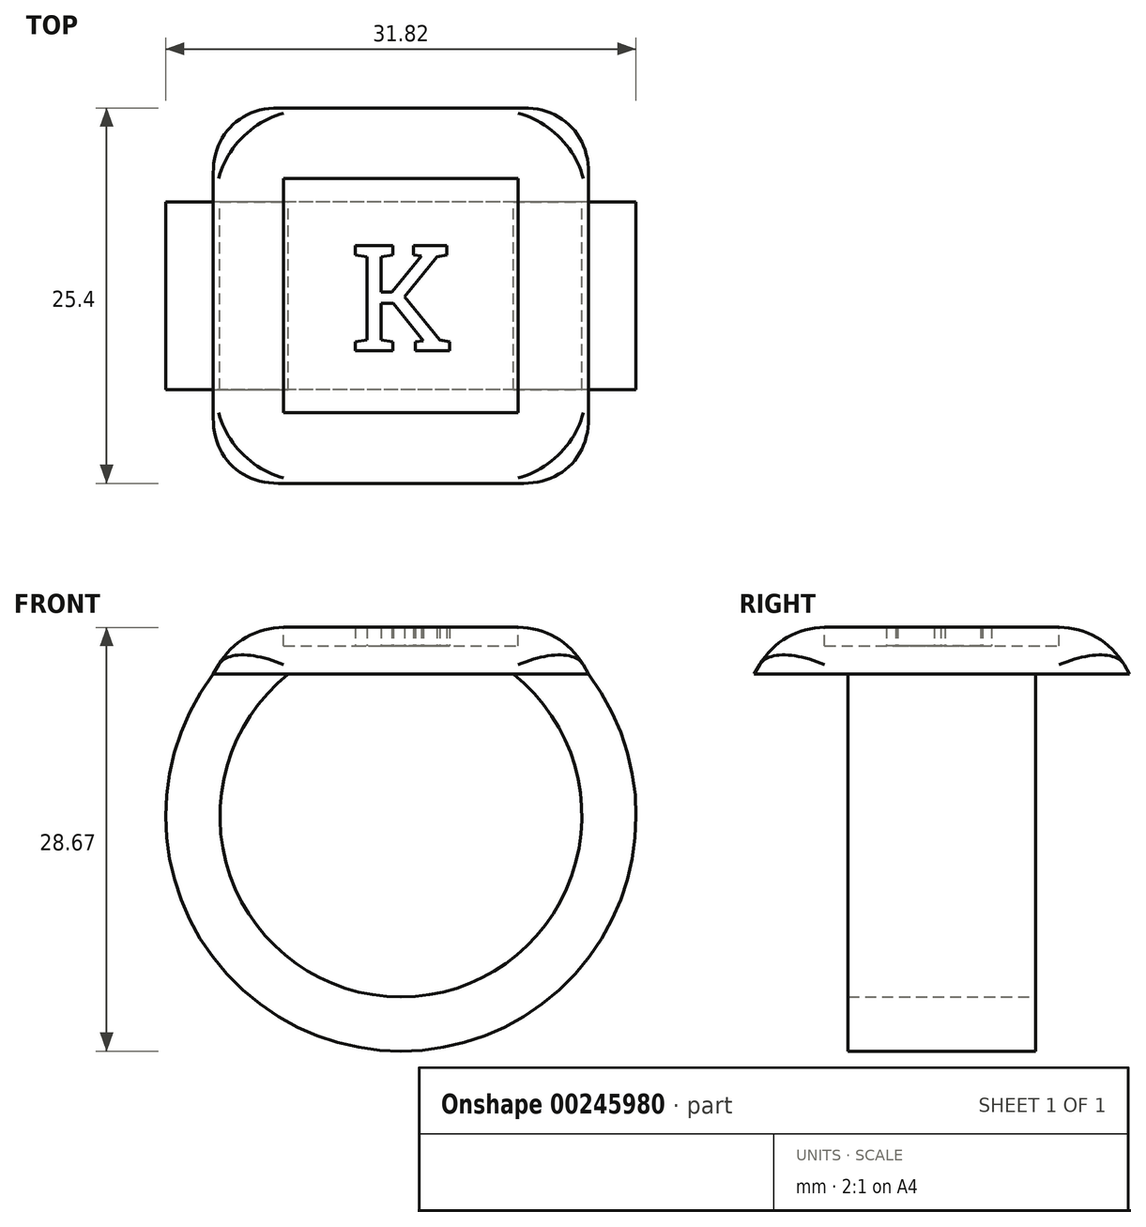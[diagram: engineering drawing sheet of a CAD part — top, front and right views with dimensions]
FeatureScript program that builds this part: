
annotation { "Feature Type Name" : "Feature", "Feature Type Description" : "" }
export const myFeature = defineFeature(function(context is Context, id is Id, definition is map)
    precondition{}
    {
        {
            var Q0;
            Q0=qCreatedBy(makeId("Top.planeOp"),FACE);
            var sketch = newSketch(context, id + "F0", { "sketchPlane" : qUnion([Q0])});
            skLineSegment(sketch, "E0.bottom", {"start": v(12.7, 12.7) * mm, "end": v(-12.7, 12.7) * mm});
            skLineSegment(sketch, "E0.top", {"start": v(12.7, -12.7) * mm, "end": v(-12.7, -12.7) * mm});
            skLineSegment(sketch, "E0.left", {"start": v(12.7, 12.7) * mm, "end": v(12.7, -12.7) * mm});
            skLineSegment(sketch, "E0.right", {"start": v(-12.7, 12.7) * mm, "end": v(-12.7, -12.7) * mm});
            skPoint(sketch, "E0.middle", {"position": v(0, 0) * mm});
            skSolve(sketch);
        }
        {
            var Q0;
            Q0=makeQuery(id+"F0.imprint","IMPRINT",FACE,{"disambiguationData":[TD([[makeQuery(id+"F0.imprint","IMPRINT",EDGE,{"derivedFrom":sQuery(id+"F0.wireOp",EDGE,"E0.bottom")}),1.0]])]});
            extrude(context, id + "F1", {"entities" : qUnion([Q0]), "depth" : 3.17 * mm, "hasDraft" : true, "draftAngle" : 30 * degree, "draftPullDirection" : true});
        }
        {
            var Q0;
            Q0=qCreatedBy(makeId("Front.planeOp"),FACE);
            var sketch = newSketch(context, id + "F2", { "sketchPlane" : qUnion([Q0])});
            skArc(sketch, "E1", {"start": v(-10.16, 0) * mm, "mid": v(0, -23.56) * mm, "end": v(10.16, 0) * mm});
            skSolve(sketch);
        }
        {
            var Q0;
            Q0=qCreatedBy(makeId("Top.planeOp"),FACE);
            var sketch = newSketch(context, id + "F3", { "sketchPlane" : qUnion([Q0])});
            skLineSegment(sketch, "E2.bottom", {"start": v(12.7, -6.35) * mm, "end": v(7.62, -6.35) * mm});
            skLineSegment(sketch, "E2.top", {"start": v(12.7, 6.35) * mm, "end": v(7.62, 6.35) * mm});
            skLineSegment(sketch, "E2.left", {"start": v(12.7, -6.35) * mm, "end": v(12.7, 6.35) * mm});
            skLineSegment(sketch, "E2.right", {"start": v(7.62, -6.35) * mm, "end": v(7.62, 6.35) * mm});
            skPoint(sketch, "E2.middle", {"position": v(10.16, 0) * mm});
            skSolve(sketch);
        }
        {
            var Q0;
            Q0=makeQuery(id+"F3.imprint","IMPRINT",FACE,{"disambiguationData":[TD([[makeQuery(id+"F3.imprint","IMPRINT",EDGE,{"derivedFrom":sQuery(id+"F3.wireOp",EDGE,"E2.bottom")}),-1.0]])]});
            var Q1;
            Q1=sQuery(id+"F2.wireOp",EDGE,"E1");
            sweep(context, id + "F4", {"operationType" : NewBodyOperationType.ADD, "profiles" : qUnion([Q0]), "path" : qUnion([Q1])});
        }
        {
            var Q0;
            Q0=qCreatedBy(makeId("Front.planeOp"),FACE);
            var sketch = newSketch(context, id + "F5", { "sketchPlane" : qUnion([Q0])});
            skArc(sketch, "E3", {"start": v(-7.62, 0) * mm, "mid": v(-8.9, -1.18) * mm, "end": v(-10.01, -2.54) * mm});
            skLineSegment(sketch, "E4.0", {"start": v(-7.62, 0) * mm, "end": v(-10.16, 0) * mm});
            skLineSegment(sketch, "E5.0", {"start": v(-10.16, 0) * mm, "end": v(-10.01, -2.54) * mm});
            skPoint(sketch, "E6.orphan", {"position": v(12.7, 0) * mm});
            skPoint(sketch, "E7.orphan", {"position": v(-12.7, 0) * mm});
            skSolve(sketch);
        }
        {
            var Q0;
            Q0 = qSketchRegion(id + "F5", true);
            var Q1;
            Q1=sQuery(id+"F5.wireOp",EDGE,"E3");
            extrude(context, id + "F6", {"entities" : qUnion([Q0]), "operationType" : NewBodyOperationType.ADD, "surfaceEntities" : qUnion([Q1]), "endBound" : BoundingType.SYMMETRIC, "depth" : 12.7 * mm});
        }
        {
            var Q0;
            Q0=makeQuery(id+"F1.opExtrude","SWEPT_EDGE",EDGE,{"disambiguationData":[OSD([sQuery(id+"F0.wireOp",EDGE,"E0.top"),sQuery(id+"F0.wireOp",EDGE,"E0.right")])]});
            var Q1;
            Q1=makeQuery(id+"F1.opExtrude","SWEPT_EDGE",EDGE,{"disambiguationData":[OSD([sQuery(id+"F0.wireOp",EDGE,"E0.top"),sQuery(id+"F0.wireOp",EDGE,"E0.left")])]});
            var Q2;
            Q2=makeQuery(id+"F1.opExtrude","SWEPT_EDGE",EDGE,{"disambiguationData":[OSD([sQuery(id+"F0.wireOp",EDGE,"E0.bottom"),sQuery(id+"F0.wireOp",EDGE,"E0.left")])]});
            var Q3;
            Q3=makeQuery(id+"F1.opExtrude","SWEPT_EDGE",EDGE,{"disambiguationData":[OSD([sQuery(id+"F0.wireOp",EDGE,"E0.bottom"),sQuery(id+"F0.wireOp",EDGE,"E0.right")])]});
            var Q4;
            Q4=makeQuery(id+"F1.opExtrude","CAP_FACE",FACE,{"disambiguationData":[OSD([sQuery(id+"F0.wireOp",EDGE,"E0.bottom"),sQuery(id+"F0.wireOp",EDGE,"E0.top"),sQuery(id+"F0.wireOp",EDGE,"E0.left"),sQuery(id+"F0.wireOp",EDGE,"E0.right")])],"isStart":false});
            fillet(context, id + "F7", {"entities" : qUnion([Q0, Q1, Q2, Q3, Q4]), "radius" : 5.08 * mm, "tangentPropagation" : true, "allowEdgeOverflow" : false});
        }
        {
            var Q0;
            Q0=makeQuery(id+"F1.opExtrude","CAP_FACE",FACE,{"disambiguationData":[OSD([sQuery(id+"F0.wireOp",EDGE,"E0.bottom"),sQuery(id+"F0.wireOp",EDGE,"E0.top"),sQuery(id+"F0.wireOp",EDGE,"E0.left"),sQuery(id+"F0.wireOp",EDGE,"E0.right")])],"isStart":false});
            var sketch = newSketch(context, id + "F8", { "sketchPlane" : qUnion([Q0])});
            skLineSegment(sketch, "E8.0", {"start": v(-8.19, 8.19) * mm, "end": v(-8.19, -8.19) * mm});
            skLineSegment(sketch, "E8.1", {"start": v(8.19, 8.19) * mm, "end": v(-8.19, 8.19) * mm});
            skLineSegment(sketch, "E8.2", {"start": v(8.19, -8.19) * mm, "end": v(8.19, 8.19) * mm});
            skLineSegment(sketch, "E8.3", {"start": v(-8.19, -8.19) * mm, "end": v(8.19, -8.19) * mm});
            skSolve(sketch);
        }
        {
            var Q0;
            {var subQ0=sQuery(id+"F0.wireOp",EDGE,"E0.right");var subQ1=sQuery(id+"F0.wireOp",EDGE,"E0.left");var subQ2=sQuery(id+"F0.wireOp",EDGE,"E0.top");var subQ3=sQuery(id+"F0.wireOp",EDGE,"E0.bottom");var subQ4=makeQuery(id+"F1.opExtrude","CAP_FACE",FACE,{"disambiguationData":[OSD([subQ3,subQ2,subQ1,subQ0])],"isStart":false});Q0=makeQuery(id+"F8.imprint","IMPRINT",FACE,{"disambiguationData":[TD([[makeQuery(id+"F8.imprint","IMPRINT",EDGE,{"derivedFrom":makeQuery(id+"F7.opFillet","BLEND_EDGE",EDGE,{"blendedFrom":[makeQuery(id+"F1.opExtrude","CAP_EDGE",EDGE,{"disambiguationData":[OSD([subQ3])],"isStart":false}),subQ4],"blendedInto":[subQ4]})}),1.0]])]});}
            extrude(context, id + "F9", {"entities" : qUnion([Q0]), "operationType" : NewBodyOperationType.REMOVE, "oppositeDirection" : true, "depth" : 1.27 * mm});
        }
        {
            var Q0;
            Q0=makeQuery(id+"F9.boolean.opBoolean","COPY",FACE,{"derivedFrom":makeQuery(id+"F9.opExtrude","CAP_FACE",FACE,{"disambiguationData":[OSD([sQuery(id+"F0.wireOp",EDGE,"E0.bottom"),sQuery(id+"F0.wireOp",EDGE,"E0.top"),sQuery(id+"F0.wireOp",EDGE,"E0.left"),sQuery(id+"F0.wireOp",EDGE,"E0.right")])],"isStart":false})});
            var sketch = newSketch(context, id + "F10", { "sketchPlane" : qUnion([Q0])});
            skText(sketch, "E9", { "text": "K", "fontName": "RobotoSlab-Regular.ttf"});
            const initialGuessF10  = {"E9": [-0.00345, -0.00374, 1, 0, 0.0072]};
            skSetInitialGuess(sketch, initialGuessF10);
            skSolve(sketch);
        }
        {
            var Q0;
            Q0 = qSketchRegion(id + "F10", true);
            extrude(context, id + "F11", {"entities" : qUnion([Q0]), "operationType" : NewBodyOperationType.ADD, "depth" : 1.27 * mm});
        }
    });
